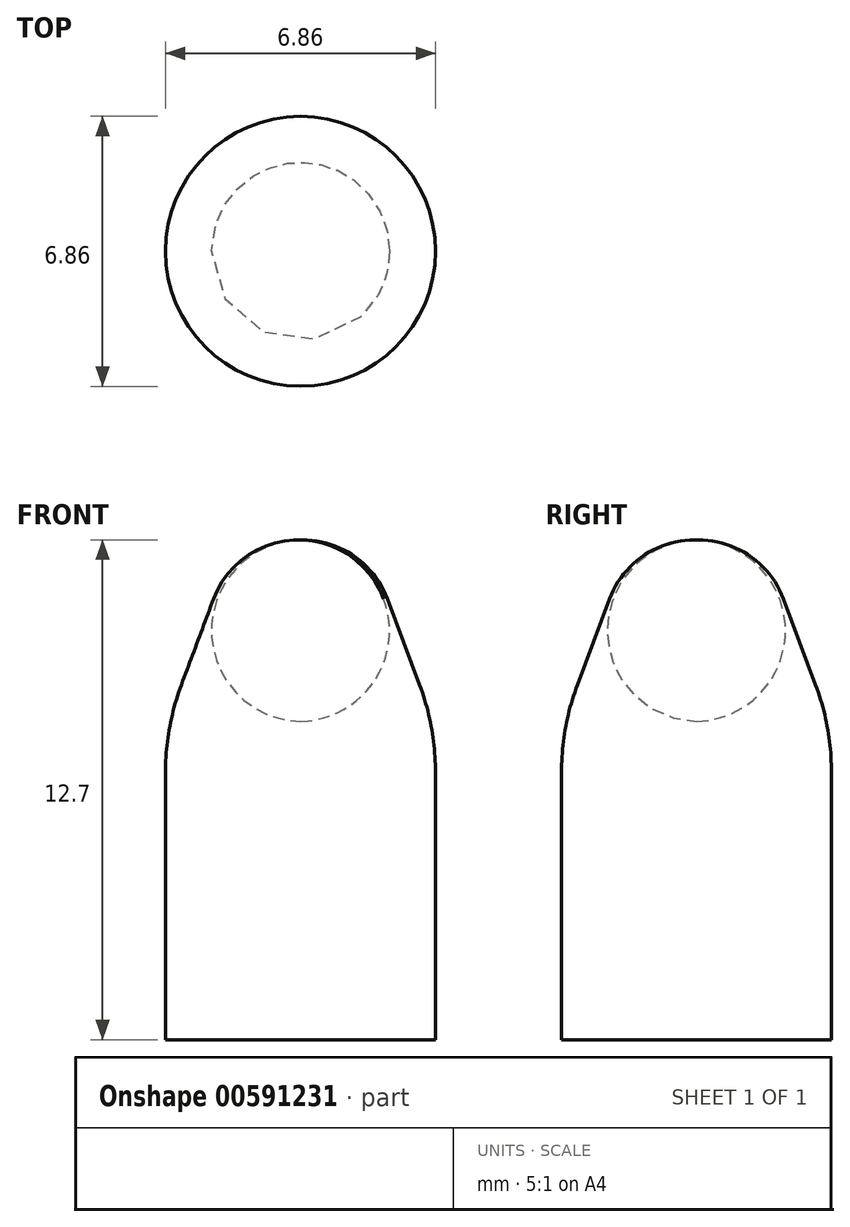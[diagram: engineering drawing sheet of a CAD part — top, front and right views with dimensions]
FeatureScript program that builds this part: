
annotation { "Feature Type Name" : "Feature", "Feature Type Description" : "" }
export const myFeature = defineFeature(function(context is Context, id is Id, definition is map)
    precondition{}
    {
        {
            var Q0;
            Q0=qCreatedBy(makeId("Front.planeOp"),FACE);
            var sketch = newSketch(context, id + "F0", { "sketchPlane" : qUnion([Q0])});
            skLineSegment(sketch, "E0", {"start": v(0, 0) * mm, "end": v(0, 12.7) * mm});
            skLineSegment(sketch, "E1", {"start": v(0, 0) * mm, "end": v(-3.43, 0) * mm});
            skLineSegment(sketch, "E2", {"start": v(-3.43, 0) * mm, "end": v(-3.43, 6.79) * mm});
            skLineSegment(sketch, "E3", {"start": v(-3.03, 9.01) * mm, "end": v(-2.2, 11.2) * mm});
            skArc(sketch, "E4", {"start": v(0, 12.7) * mm, "mid": v(-1.34, 12.3) * mm, "end": v(-2.2, 11.2) * mm});
            skPoint(sketch, "E5.visualSharp", {"position": v(-3.43, 7.94) * mm});
            skArc(sketch, "E5.filletArc", {"start": v(-3.03, 9.01) * mm, "mid": v(-3.33, 7.92) * mm, "end": v(-3.43, 6.79) * mm});
            skSolve(sketch);
        }
        {
            var Q0;
            Q0 = qSketchRegion(id + "F0", true);
            var Q1;
            Q1=sQuery(id+"F0.wireOp",EDGE,"E0");
            revolve(context, id + "F1", {"surfaceOperationType" : NewSurfaceOperationType.NEW, "entities" : qUnion([Q0]), "axis" : qUnion([Q1]), "revolveType" : RevolveType.FULL});
        }
    });
